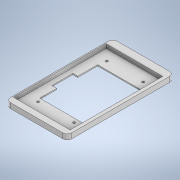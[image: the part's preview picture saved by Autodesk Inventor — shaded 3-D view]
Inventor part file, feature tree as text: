
AUTODESK INVENTOR PART (.ipt)
format: ipt  version: 2021 (Build 250183000, 183)  size: 166,400 bytes
history: native  units: mm
features: extrude x3, sketch x3, projected_geometry x1
ambient origin geometry x8: Origin, YZ Plane, XZ Plane, XY Plane, X Axis, Y Axis, Z Axis, Center Point
bodies: Solid1 (feature_tree)
feature tree (7):
  extrude  "Extrusion1"  Depth=193.2mm
  extrude  "Extrusion2"  Depth=4.2mm
  extrude  "Extrusion3"  Depth=7.5mm
  sketch  "Sketch1"  dims[d0=110.94mm d1=193.2mm]
  sketch  "Sketch2"  dims[d2=4.2mm d3=4.2mm]
  projected_geometry  "Projected Loop1"
  sketch  "Sketch3"  dims[d4=65.3mm d5=65.697mm d6=4.2mm d7=4.2mm d8=126.2mm d9=126.501mm d10=0.0mm d11=22.6mm d12=33.35mm d13=8.0mm d14=2.0mm d15=0.0mm d16=2.0mm d17=14.0mm d18=11.0mm d19=6.0mm d20=7.5mm d21=0.0mm d22=105.0mm d23=79.0mm d24=6.0mm d25=30.0mm d26=50.0mm d27=38.0mm d28=9.0mm d29=7.5mm d30=0.0mm]
